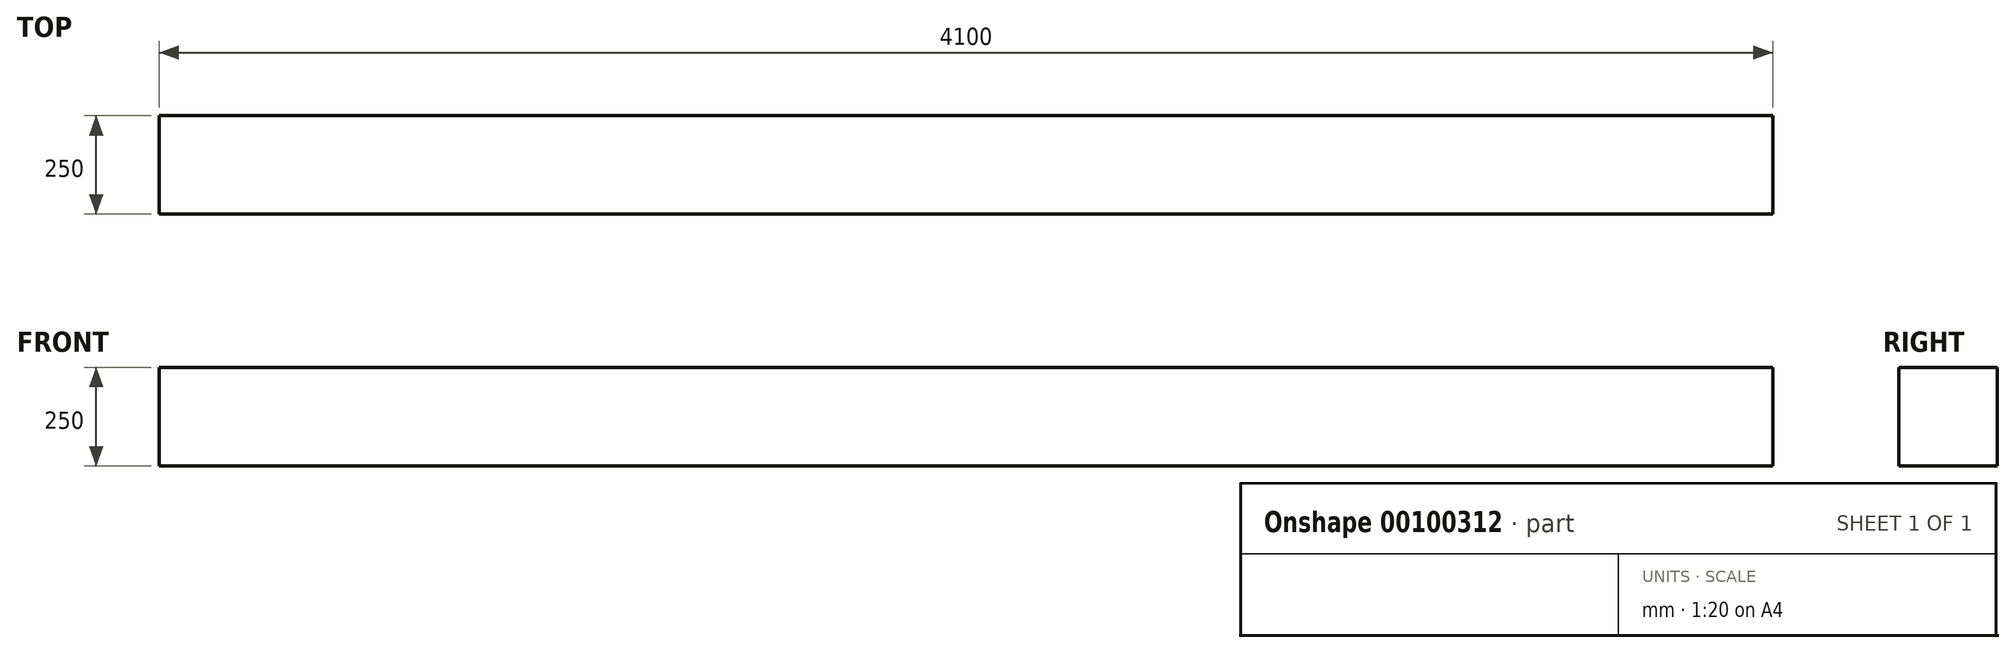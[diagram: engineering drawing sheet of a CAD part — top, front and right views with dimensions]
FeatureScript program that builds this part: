
annotation { "Feature Type Name" : "Feature", "Feature Type Description" : "" }
export const myFeature = defineFeature(function(context is Context, id is Id, definition is map)
    precondition{}
    {
        {
            var Q0;
            Q0=qCreatedBy(makeId("Top.planeOp"),FACE);
            var sketch = newSketch(context, id + "F0", { "sketchPlane" : qUnion([Q0])});
            skLineSegment(sketch, "E0.bottom", {"start": v(-1529.26, -507.7) * mm, "end": v(2570.74, -507.7) * mm});
            skLineSegment(sketch, "E0.top", {"start": v(-1529.26, -757.7) * mm, "end": v(2570.74, -757.7) * mm});
            skLineSegment(sketch, "E0.left", {"start": v(-1529.26, -507.7) * mm, "end": v(-1529.26, -757.7) * mm});
            skLineSegment(sketch, "E0.right", {"start": v(2570.74, -507.7) * mm, "end": v(2570.74, -757.7) * mm});
            skSolve(sketch);
        }
        {
            var Q0;
            Q0 = qSketchRegion(id + "F0", true);
            extrude(context, id + "F1", {"entities" : qUnion([Q0]), "depth" : 250 * mm});
        }
    });
